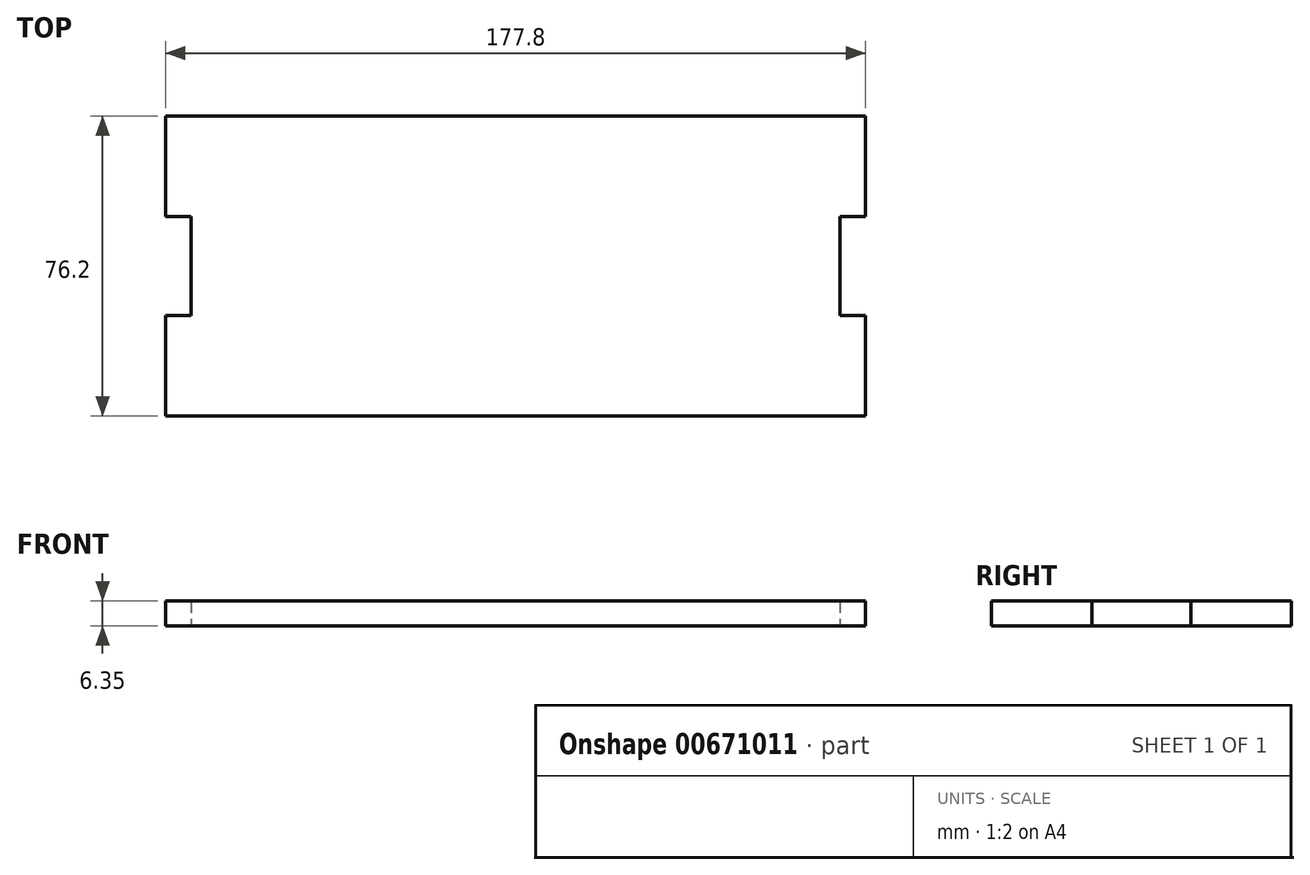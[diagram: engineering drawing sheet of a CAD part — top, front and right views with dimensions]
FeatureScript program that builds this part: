
annotation { "Feature Type Name" : "Feature", "Feature Type Description" : "" }
export const myFeature = defineFeature(function(context is Context, id is Id, definition is map)
    precondition{}
    {
        {
            var Q0;
            Q0=qCreatedBy(makeId("Top.planeOp"),FACE);
            var sketch = newSketch(context, id + "F0", { "sketchPlane" : qUnion([Q0])});
            skLineSegment(sketch, "E0.bottom", {"start": v(0, 0) * mm, "end": v(177.8, 0) * mm});
            skLineSegment(sketch, "E0.top", {"start": v(0, 76.2) * mm, "end": v(177.8, 76.2) * mm});
            skLineSegment(sketch, "E0.left", {"start": v(0, 0) * mm, "end": v(0, 76.2) * mm});
            skLineSegment(sketch, "E0.right", {"start": v(177.8, 0) * mm, "end": v(177.8, 76.2) * mm});
            skLineSegment(sketch, "E1.bottom", {"start": v(25.31, 0) * mm, "end": v(50.89, 0) * mm});
            skLineSegment(sketch, "E1.top", {"start": v(25.31, -6.53) * mm, "end": v(50.89, -6.53) * mm});
            skLineSegment(sketch, "E1.left", {"start": v(25.31, 0) * mm, "end": v(25.31, -6.53) * mm});
            skLineSegment(sketch, "E1.right", {"start": v(50.89, 0) * mm, "end": v(50.89, -6.53) * mm});
            skLineSegment(sketch, "E2.bottom", {"start": v(76.11, 0) * mm, "end": v(101.69, 0) * mm});
            skLineSegment(sketch, "E2.top", {"start": v(76.11, -6.53) * mm, "end": v(101.69, -6.53) * mm});
            skLineSegment(sketch, "E2.left", {"start": v(76.11, 0) * mm, "end": v(76.11, -6.53) * mm});
            skLineSegment(sketch, "E2.right", {"start": v(101.69, 0) * mm, "end": v(101.69, -6.53) * mm});
            skLineSegment(sketch, "E3.bottom", {"start": v(126.91, 0) * mm, "end": v(152.49, 0) * mm});
            skLineSegment(sketch, "E3.top", {"start": v(126.91, -6.53) * mm, "end": v(152.49, -6.53) * mm});
            skLineSegment(sketch, "E3.left", {"start": v(126.91, 0) * mm, "end": v(126.91, -6.53) * mm});
            skLineSegment(sketch, "E3.right", {"start": v(152.49, 0) * mm, "end": v(152.49, -6.53) * mm});
            skPoint(sketch, "E4", {"position": v(38.1, 0) * mm});
            skPoint(sketch, "E5", {"position": v(139.7, 0) * mm});
            skPoint(sketch, "E6", {"position": v(88.9, -6.53) * mm});
            skLineSegment(sketch, "E7.bottom", {"start": v(0, 50.71) * mm, "end": v(6.53, 50.71) * mm});
            skLineSegment(sketch, "E7.top", {"start": v(0, 25.49) * mm, "end": v(6.53, 25.49) * mm});
            skLineSegment(sketch, "E7.left", {"start": v(0, 50.71) * mm, "end": v(0, 25.49) * mm});
            skLineSegment(sketch, "E7.right", {"start": v(6.53, 50.71) * mm, "end": v(6.53, 25.49) * mm});
            skLineSegment(sketch, "E8.bottom", {"start": v(177.8, 50.71) * mm, "end": v(171.27, 50.71) * mm});
            skLineSegment(sketch, "E8.top", {"start": v(177.8, 25.49) * mm, "end": v(171.27, 25.49) * mm});
            skLineSegment(sketch, "E8.left", {"start": v(177.8, 50.71) * mm, "end": v(177.8, 25.49) * mm});
            skLineSegment(sketch, "E8.right", {"start": v(171.27, 50.71) * mm, "end": v(171.27, 25.49) * mm});
            skPoint(sketch, "E9", {"position": v(6.53, 38.1) * mm});
            skPoint(sketch, "E10", {"position": v(171.27, 38.1) * mm});
            skSolve(sketch);
        }
        {
            var Q0;
            {var subQ2=sQuery(id+"F0.wireOp",EDGE,"E0.top");Q0=makeQuery(id+"F0.imprint","IMPRINT",FACE,{"disambiguationData":[TD([[makeQuery(id+"F0.imprint","IMPRINT",EDGE,{"derivedFrom":subQ2}),-1.0]])]});}
            var Q1;
            Q1=makeQuery(id+"F0.imprint","IMPRINT",FACE,{"disambiguationData":[TD([[makeQuery(id+"F0.imprint","IMPRINT",EDGE,{"derivedFrom":sQuery(id+"F0.wireOp",EDGE,"E1.bottom")}),-1.0]])]});
            var Q2;
            Q2=makeQuery(id+"F0.imprint","IMPRINT",FACE,{"disambiguationData":[TD([[makeQuery(id+"F0.imprint","IMPRINT",EDGE,{"derivedFrom":sQuery(id+"F0.wireOp",EDGE,"E2.bottom")}),-1.0]])]});
            var Q3;
            Q3=makeQuery(id+"F0.imprint","IMPRINT",FACE,{"disambiguationData":[TD([[makeQuery(id+"F0.imprint","IMPRINT",EDGE,{"derivedFrom":sQuery(id+"F0.wireOp",EDGE,"E3.bottom")}),-1.0]])]});
            extrude(context, id + "F1", {"entities" : qUnion([Q0, Q1, Q2, Q3]), "depth" : 6.35 * mm, "offsetDistance" : 25.4 * mm});
        }
    });
